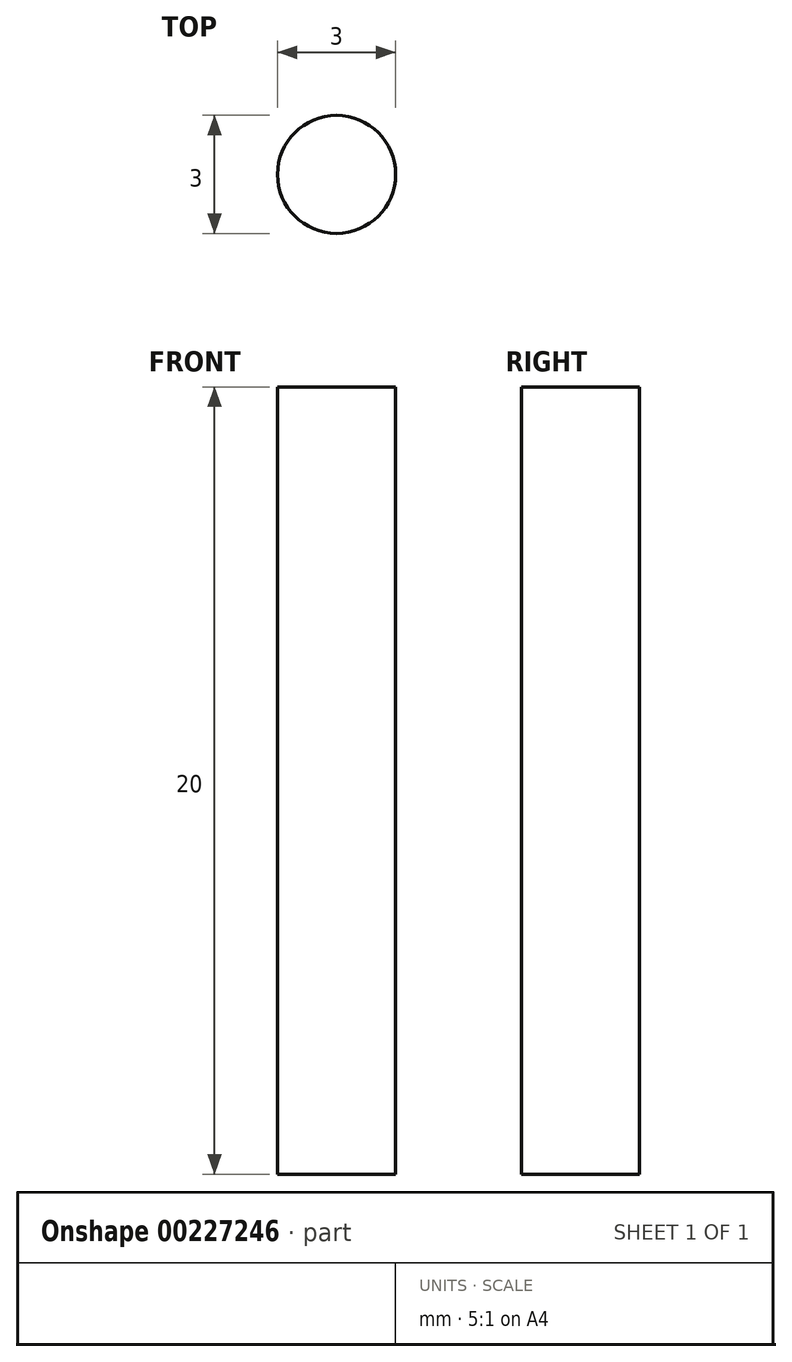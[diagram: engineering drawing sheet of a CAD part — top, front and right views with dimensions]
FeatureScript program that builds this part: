
annotation { "Feature Type Name" : "Feature", "Feature Type Description" : "" }
export const myFeature = defineFeature(function(context is Context, id is Id, definition is map)
    precondition{}
    {
        {
            var Q0;
            Q0=qCreatedBy(makeId("Top.planeOp"),FACE);
            var sketch = newSketch(context, id + "F0", { "sketchPlane" : qUnion([Q0])});
            skCircle(sketch, "E0", {"center": v(0, 0) * mm, "radius": 1.5 * mm});
            skSolve(sketch);
        }
        {
            var Q0;
            Q0 = qSketchRegion(id + "F0", true);
            extrude(context, id + "F1", {"entities" : qUnion([Q0]), "depth" : 20 * mm});
        }
    });
